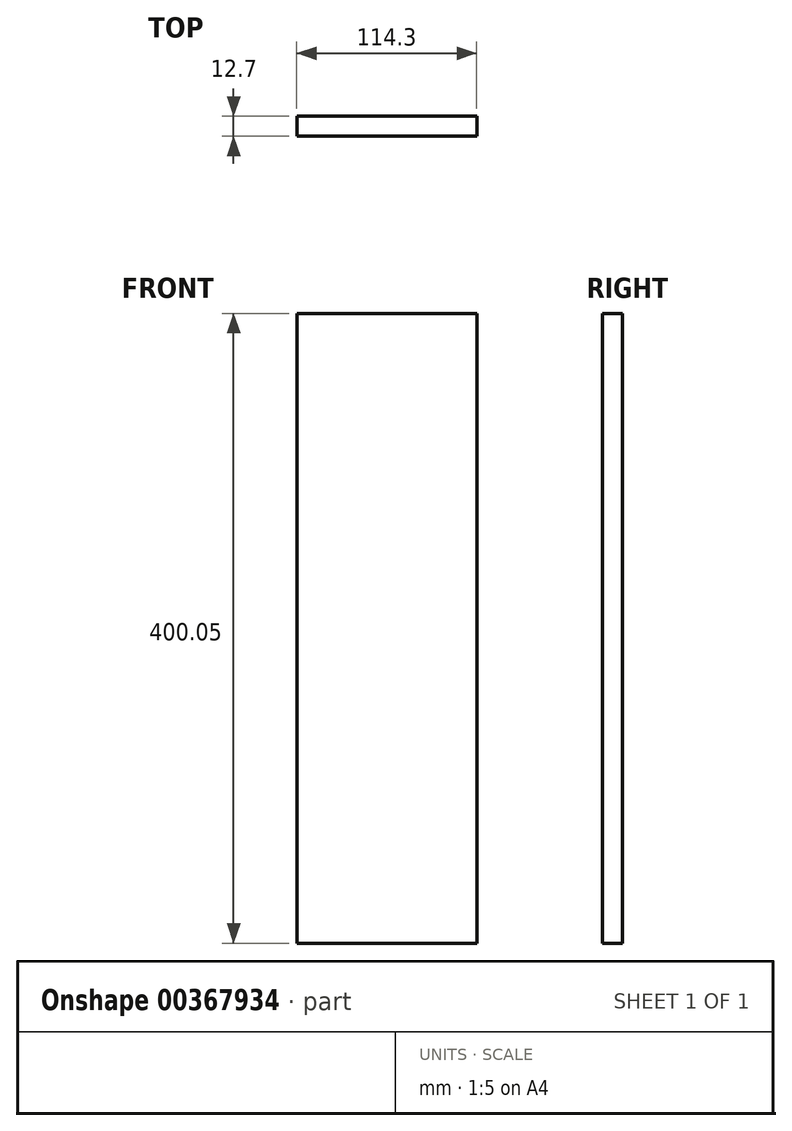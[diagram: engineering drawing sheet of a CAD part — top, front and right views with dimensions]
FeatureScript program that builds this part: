
annotation { "Feature Type Name" : "Feature", "Feature Type Description" : "" }
export const myFeature = defineFeature(function(context is Context, id is Id, definition is map)
    precondition{}
    {
        {
            var Q0;
            Q0=qCreatedBy(makeId("Front.planeOp"),FACE);
            var sketch = newSketch(context, id + "F0", { "sketchPlane" : qUnion([Q0])});
            skLineSegment(sketch, "E0.bottom", {"start": v(-59.82, 338.66) * mm, "end": v(54.48, 338.66) * mm});
            skLineSegment(sketch, "E0.top", {"start": v(-59.82, -61.4) * mm, "end": v(54.48, -61.4) * mm});
            skLineSegment(sketch, "E0.left", {"start": v(-59.82, 338.66) * mm, "end": v(-59.82, -61.4) * mm});
            skLineSegment(sketch, "E0.right", {"start": v(54.48, 338.66) * mm, "end": v(54.48, -61.4) * mm});
            skSolve(sketch);
        }
        {
            var Q0;
            Q0=makeQuery(id+"F0.imprint","IMPRINT",FACE,{"disambiguationData":[TD([[makeQuery(id+"F0.imprint","IMPRINT",EDGE,{"derivedFrom":sQuery(id+"F0.wireOp",EDGE,"E0.bottom")}),-1.0]])]});
            extrude(context, id + "F1", {"entities" : qUnion([Q0]), "depth" : 12.7 * mm});
        }
    });
